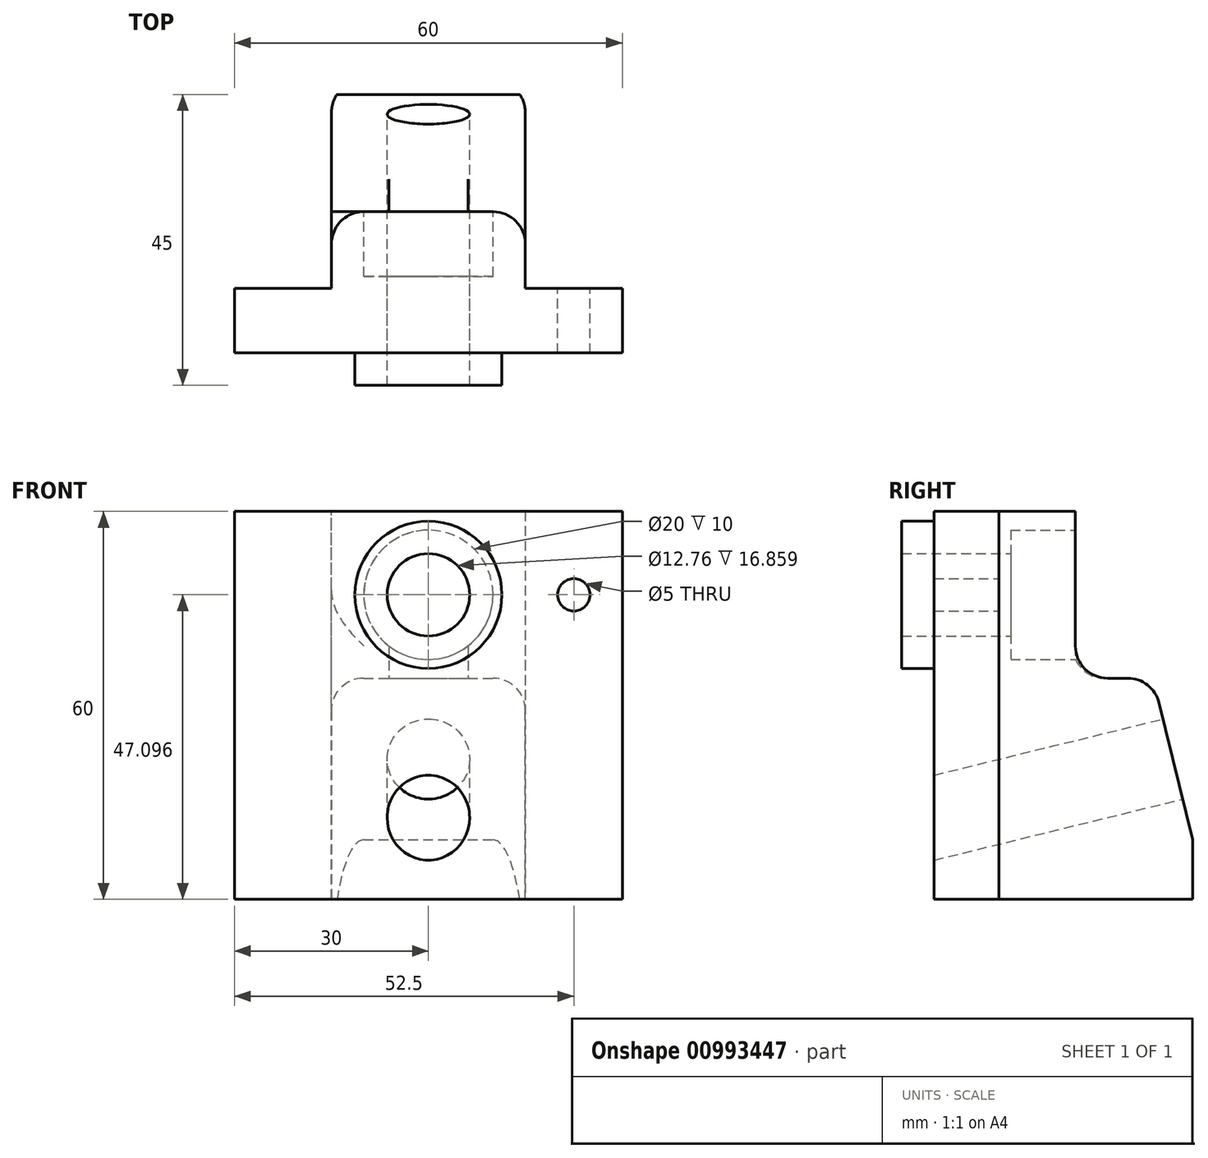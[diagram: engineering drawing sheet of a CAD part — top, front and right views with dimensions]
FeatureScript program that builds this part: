
annotation { "Feature Type Name" : "Feature", "Feature Type Description" : "" }
export const myFeature = defineFeature(function(context is Context, id is Id, definition is map)
    precondition{}
    {
        {
            var Q0;
            Q0=qCreatedBy(makeId("Right.planeOp"),FACE);
            var sketch = newSketch(context, id + "F0", { "sketchPlane" : qUnion([Q0])});
            skLineSegment(sketch, "E0", {"start": v(0, 0) * mm, "end": v(40, 0) * mm});
            skLineSegment(sketch, "E1", {"start": v(40, 0) * mm, "end": v(40, 60) * mm});
            skLineSegment(sketch, "E2", {"start": v(40, 60) * mm, "end": v(0, 60) * mm});
            skLineSegment(sketch, "E3", {"start": v(0, 60) * mm, "end": v(0, 0) * mm});
            skSolve(sketch);
        }
        {
            var Q0;
            Q0 = qSketchRegion(id + "F0", true);
            extrude(context, id + "F1", {"entities" : qUnion([Q0]), "depth" : 60 * mm, "offsetDistance" : 25 * mm});
        }
        {
            var Q0;
            Q0=qCreatedBy(makeId("Right.planeOp"),FACE);
            cPlane(context, id + "F2", {"entities" : qUnion([Q0]), "cplaneType" : CPlaneType.OFFSET, "offset" : 30 * mm, "width" : 150 * mm, "height" : 150 * mm});
        }
        {
            var Q0;
            Q0=makeQuery(id+"F1.opExtrude","CAP_FACE",FACE,{"disambiguationData":[OSD([sQuery(id+"F0.wireOp",EDGE,"E0"),sQuery(id+"F0.wireOp",EDGE,"E1"),sQuery(id+"F0.wireOp",EDGE,"E2"),sQuery(id+"F0.wireOp",EDGE,"E3")])],"isStart":false});
            var sketch = newSketch(context, id + "F3", { "sketchPlane" : qUnion([Q0])});
            skLineSegment(sketch, "E4", {"start": v(33.86, 34.2) * mm, "end": v(40, 9.2) * mm});
            skLineSegment(sketch, "E5", {"start": v(40, 9.2) * mm, "end": v(40, 60) * mm});
            skLineSegment(sketch, "E6", {"start": v(33.86, 34.2) * mm, "end": v(21.86, 34.2) * mm});
            skLineSegment(sketch, "E7", {"start": v(21.86, 34.2) * mm, "end": v(21.86, 60) * mm});
            skLineSegment(sketch, "E8", {"start": v(21.86, 60) * mm, "end": v(40, 60) * mm});
            skSolve(sketch);
        }
        {
            var Q0;
            Q0 = qSketchRegion(id + "F3", true);
            extrude(context, id + "F4", {"entities" : qUnion([Q0]), "operationType" : NewBodyOperationType.REMOVE, "endBound" : BoundingType.THROUGH_ALL, "oppositeDirection" : true, "depth" : 25 * mm, "offsetDistance" : 25 * mm});
        }
        {
            var Q0;
            Q0=makeQuery(id+"F4.boolean.opBoolean","COPY",FACE,{"derivedFrom":makeQuery(id+"F4.opExtrude","SWEPT_FACE",FACE,{"disambiguationData":[OSD([sQuery(id+"F3.wireOp",EDGE,"E4")])]})});
            var sketch = newSketch(context, id + "F5", { "sketchPlane" : qUnion([Q0])});
            skCircle(sketch, "E9", {"center": v(-30, 12.26) * mm, "radius": 6.38 * mm});
            skSolve(sketch);
        }
        {
            var Q0;
            Q0 = qSketchRegion(id + "F5", true);
            extrude(context, id + "F6", {"entities" : qUnion([Q0]), "operationType" : NewBodyOperationType.REMOVE, "endBound" : BoundingType.THROUGH_ALL, "oppositeDirection" : true, "depth" : 25 * mm, "offsetDistance" : 25 * mm});
        }
        {
            var Q0;
            Q0=makeQuery(id+"F4.boolean.opBoolean","COPY",FACE,{"derivedFrom":makeQuery(id+"F4.opExtrude","SWEPT_FACE",FACE,{"disambiguationData":[OSD([sQuery(id+"F3.wireOp",EDGE,"E7")])]})});
            var sketch = newSketch(context, id + "F7", { "sketchPlane" : qUnion([Q0])});
            skCircle(sketch, "E10", {"center": v(-30, 47.1) * mm, "radius": 10 * mm});
            skSolve(sketch);
        }
        {
            var Q0;
            Q0 = qSketchRegion(id + "F7", true);
            extrude(context, id + "F8", {"entities" : qUnion([Q0]), "operationType" : NewBodyOperationType.REMOVE, "oppositeDirection" : true, "depth" : 10 * mm, "offsetDistance" : 25 * mm});
        }
        {
            var Q0;
            Q0=makeQuery(id+"F8.boolean.opBoolean","COPY",FACE,{"derivedFrom":makeQuery(id+"F8.opExtrude","CAP_FACE",FACE,{"disambiguationData":[OSD([sQuery(id+"F7.wireOp",EDGE,"E10")])],"isStart":false})});
            var sketch = newSketch(context, id + "F9", { "sketchPlane" : qUnion([Q0])});
            skCircle(sketch, "E11", {"center": v(-30, 47.1) * mm, "radius": 6.38 * mm});
            skSolve(sketch);
        }
        {
            var Q0;
            Q0 = qSketchRegion(id + "F9", true);
            extrude(context, id + "F10", {"entities" : qUnion([Q0]), "operationType" : NewBodyOperationType.REMOVE, "endBound" : BoundingType.THROUGH_ALL, "oppositeDirection" : true, "depth" : 25 * mm, "offsetDistance" : 25 * mm});
        }
        {
            var Q0;
            Q0=makeQuery(id+"F1.opExtrude","SWEPT_FACE",FACE,{"disambiguationData":[OSD([sQuery(id+"F0.wireOp",EDGE,"E1")])]});
            var sketch = newSketch(context, id + "F11", { "sketchPlane" : qUnion([Q0])});
            skLineSegment(sketch, "E12", {"start": v(-60, 0) * mm, "end": v(-60, 60) * mm});
            skLineSegment(sketch, "E13", {"start": v(-60, 60) * mm, "end": v(-45, 60) * mm});
            skLineSegment(sketch, "E14", {"start": v(-45, 60) * mm, "end": v(-45, 0) * mm});
            skLineSegment(sketch, "E15", {"start": v(-15, 0) * mm, "end": v(-15, 60) * mm});
            skLineSegment(sketch, "E16", {"start": v(-15, 60) * mm, "end": v(0, 60) * mm});
            skLineSegment(sketch, "E17", {"start": v(0, 60) * mm, "end": v(0, 0) * mm});
            skLineSegment(sketch, "E18", {"start": v(0, 0) * mm, "end": v(-15, 0) * mm});
            skLineSegment(sketch, "E19.trimOffspring", {"start": v(-45, 0) * mm, "end": v(-60, 0) * mm});
            skSolve(sketch);
        }
        {
            var Q0;
            Q0 = qSketchRegion(id + "F11", true);
            extrude(context, id + "F12", {"entities" : qUnion([Q0]), "operationType" : NewBodyOperationType.REMOVE, "oppositeDirection" : true, "depth" : 30 * mm, "offsetDistance" : 25 * mm});
        }
        {
            var Q0;
            Q0=makeQuery(id+"F12.boolean.opBoolean","COPY",FACE,{"derivedFrom":makeQuery(id+"F12.opExtrude","CAP_FACE",FACE,{"disambiguationData":[OSD([sQuery(id+"F11.wireOp",EDGE,"E12"),sQuery(id+"F11.wireOp",EDGE,"E13"),sQuery(id+"F11.wireOp",EDGE,"E14"),sQuery(id+"F11.wireOp",EDGE,"E19.trimOffspring")])],"isStart":false})});
            var sketch = newSketch(context, id + "F13", { "sketchPlane" : qUnion([Q0])});
            skPoint(sketch, "E20", {"position": v(-52.5, 47.1) * mm});
            skSolve(sketch);
        }
        {
            var Q0;
            Q0=sQuery(id+"F13.wireOp",VERTEX,"E20");
            var Q1;
            Q1=sQuery(id+"F13.wireOp",VERTEX,"d77209ba-ca93-4465-8f15-18b4c2743c4e");
            var Q2;
            Q2=makeQuery(id+"F1.opExtrude","SWEPT_BODY",BODY,{"disambiguationData":[OSD([sQuery(id+"F0.wireOp",EDGE,"E0"),sQuery(id+"F0.wireOp",EDGE,"E1"),sQuery(id+"F0.wireOp",EDGE,"E2"),sQuery(id+"F0.wireOp",EDGE,"E3")])]});
            hole(context, id + "F14", {"style" : HoleStyle.SIMPLE, "endStyle" : HoleEndStyle.THROUGH, "holeDiameter" : 5 * mm, "majorDiameter" : 5 * mm, "isTappedThrough" : true, "tappedDepth" : 12 * mm, "tapClearance" : 3, "locations" : qUnion([Q0, Q1]), "scope" : qUnion([Q2])});
        }
        {
            var Q0;
            Q0=makeQuery(id+"F1.opExtrude","SWEPT_FACE",FACE,{"disambiguationData":[OSD([sQuery(id+"F0.wireOp",EDGE,"E3")])]});
            var sketch = newSketch(context, id + "F15", { "sketchPlane" : qUnion([Q0])});
            skCircle(sketch, "E21", {"center": v(30, 47.1) * mm, "radius": 6.38 * mm});
            skCircle(sketch, "E22.0", {"center": v(30, 47.1) * mm, "radius": 11.38 * mm});
            skSolve(sketch);
        }
        {
            var Q0;
            Q0 = qSketchRegion(id + "F15", true);
            extrude(context, id + "F16", {"entities" : qUnion([Q0]), "operationType" : NewBodyOperationType.ADD, "depth" : 5 * mm, "offsetDistance" : 25 * mm});
        }
        {
            var Q0;
            Q0=makeQuery(id+"F12.boolean.opBoolean","INTERSECT",EDGE,{"derivedFrom":[makeQuery(id+"F4.boolean.opBoolean","COPY",FACE,{"derivedFrom":makeQuery(id+"F4.opExtrude","SWEPT_FACE",FACE,{"disambiguationData":[OSD([sQuery(id+"F3.wireOp",EDGE,"E4")])]})}),makeQuery(id+"F12.opExtrude","SWEPT_FACE",FACE,{"disambiguationData":[OSD([sQuery(id+"F11.wireOp",EDGE,"E14")])]})]});
            var Q1;
            Q1=makeQuery(id+"F4.boolean.opBoolean","COPY",EDGE,{"derivedFrom":makeQuery(id+"F4.opExtrude","SWEPT_EDGE",EDGE,{"disambiguationData":[OSD([sQuery(id+"F3.wireOp",EDGE,"E4"),sQuery(id+"F3.wireOp",EDGE,"E6")])]})});
            var Q2;
            Q2=makeQuery(id+"F4.boolean.opBoolean","COPY",EDGE,{"derivedFrom":makeQuery(id+"F4.opExtrude","SWEPT_EDGE",EDGE,{"disambiguationData":[OSD([sQuery(id+"F0.wireOp",EDGE,"E1"),sQuery(id+"F3.wireOp",EDGE,"E4"),sQuery(id+"F3.wireOp",EDGE,"E5")])]})});
            var Q3;
            Q3=makeQuery(id+"F12.boolean.opBoolean","INTERSECT",EDGE,{"derivedFrom":[makeQuery(id+"F4.boolean.opBoolean","COPY",FACE,{"derivedFrom":makeQuery(id+"F4.opExtrude","SWEPT_FACE",FACE,{"disambiguationData":[OSD([sQuery(id+"F3.wireOp",EDGE,"E4")])]})}),makeQuery(id+"F12.opExtrude","SWEPT_FACE",FACE,{"disambiguationData":[OSD([sQuery(id+"F11.wireOp",EDGE,"E15")])]})]});
            var Q4;
            Q4=makeQuery(id+"F12.boolean.opBoolean","INTERSECT",EDGE,{"derivedFrom":[makeQuery(id+"F4.boolean.opBoolean","COPY",FACE,{"derivedFrom":makeQuery(id+"F4.opExtrude","SWEPT_FACE",FACE,{"disambiguationData":[OSD([sQuery(id+"F3.wireOp",EDGE,"E6")])]})}),makeQuery(id+"F12.opExtrude","SWEPT_FACE",FACE,{"disambiguationData":[OSD([sQuery(id+"F11.wireOp",EDGE,"E15")])]})]});
            var Q5;
            Q5=makeQuery(id+"F12.boolean.opBoolean","INTERSECT",EDGE,{"derivedFrom":[makeQuery(id+"F4.boolean.opBoolean","COPY",FACE,{"derivedFrom":makeQuery(id+"F4.opExtrude","SWEPT_FACE",FACE,{"disambiguationData":[OSD([sQuery(id+"F3.wireOp",EDGE,"E6")])]})}),makeQuery(id+"F12.opExtrude","SWEPT_FACE",FACE,{"disambiguationData":[OSD([sQuery(id+"F11.wireOp",EDGE,"E14")])]})]});
            var Q6;
            Q6=makeQuery(id+"F12.boolean.opBoolean","INTERSECT",EDGE,{"derivedFrom":[makeQuery(id+"F4.boolean.opBoolean","COPY",FACE,{"derivedFrom":makeQuery(id+"F4.opExtrude","SWEPT_FACE",FACE,{"disambiguationData":[OSD([sQuery(id+"F3.wireOp",EDGE,"E7")])]})}),makeQuery(id+"F12.opExtrude","SWEPT_FACE",FACE,{"disambiguationData":[OSD([sQuery(id+"F11.wireOp",EDGE,"E14")])]})]});
            var Q7;
            Q7=makeQuery(id+"F4.boolean.opBoolean","COPY",EDGE,{"derivedFrom":makeQuery(id+"F4.opExtrude","SWEPT_EDGE",EDGE,{"disambiguationData":[OSD([sQuery(id+"F3.wireOp",EDGE,"E6"),sQuery(id+"F3.wireOp",EDGE,"E7")])]})});
            var Q8;
            Q8=makeQuery(id+"F12.boolean.opBoolean","COPY",EDGE,{"derivedFrom":makeQuery(id+"F12.opExtrude","SWEPT_EDGE",EDGE,{"disambiguationData":[OSD([sQuery(id+"F11.wireOp",EDGE,"E15"),sQuery(id+"F11.wireOp",EDGE,"E16")])]})});
            fillet(context, id + "F17", {"entities" : qUnion([Q0, Q1, Q2, Q3, Q4, Q5, Q6, Q7, Q8]), "radius" : 5 * mm, "tangentPropagation" : true, "allowEdgeOverflow" : false});
        }
    });
